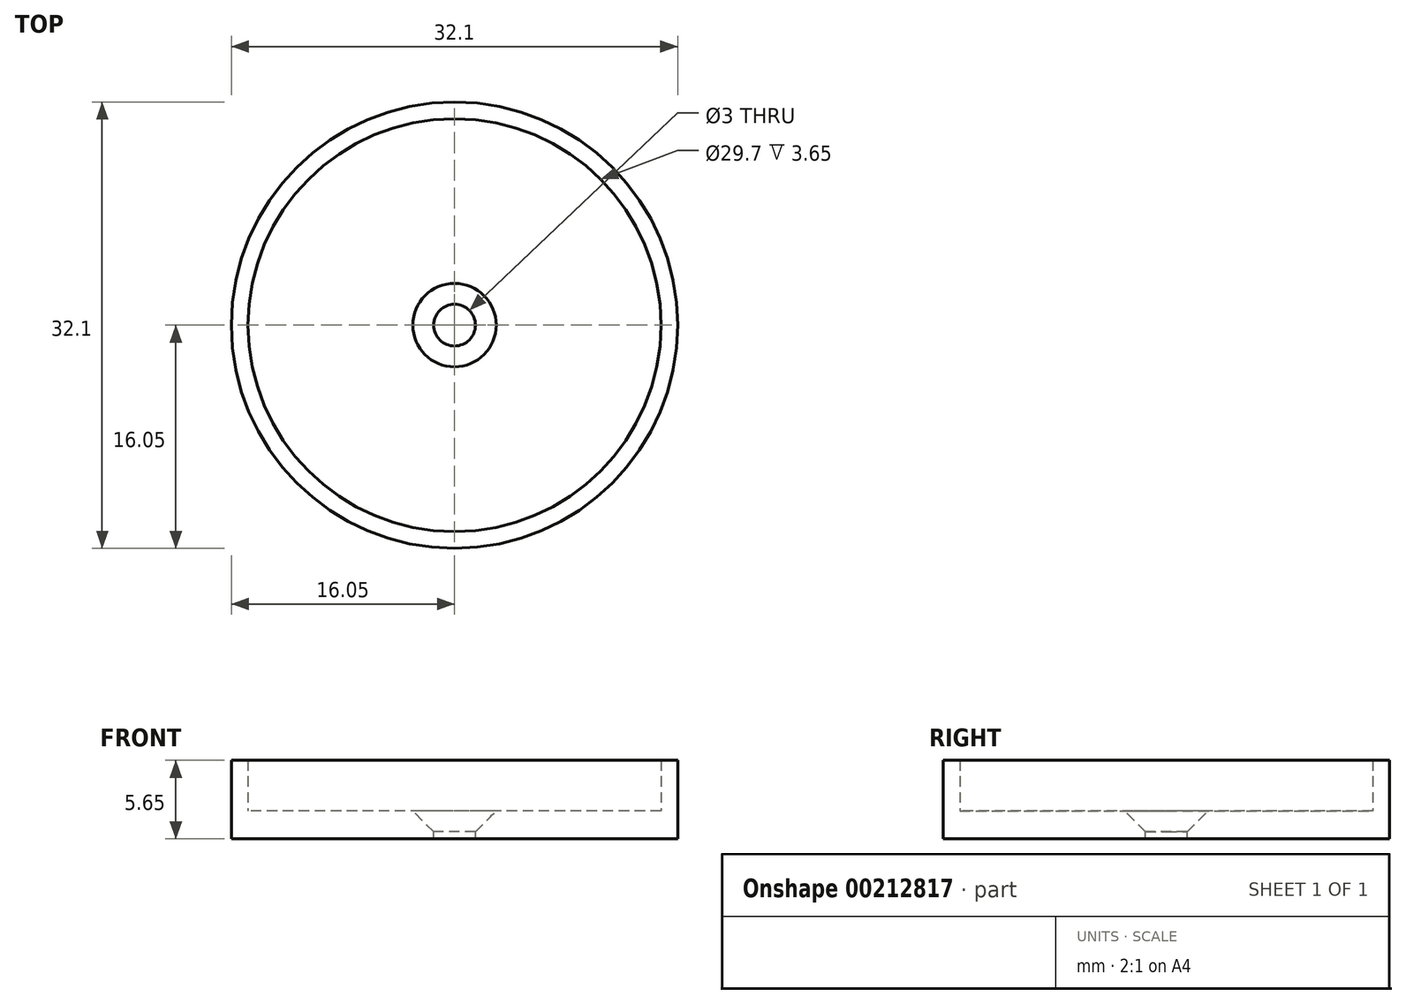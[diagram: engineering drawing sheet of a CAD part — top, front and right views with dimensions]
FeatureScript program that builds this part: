
annotation { "Feature Type Name" : "Feature", "Feature Type Description" : "" }
export const myFeature = defineFeature(function(context is Context, id is Id, definition is map)
    precondition{}
    {
        {
            var Q0;
            Q0=qCreatedBy(makeId("Top.planeOp"),FACE);
            var sketch = newSketch(context, id + "F0", { "sketchPlane" : qUnion([Q0])});
            skCircle(sketch, "E0", {"center": v(0, 0) * mm, "radius": 16.05 * mm});
            skCircle(sketch, "E1", {"center": v(0, 0) * mm, "radius": 14.85 * mm});
            skCircle(sketch, "E2", {"center": v(0, 0) * mm, "radius": 1.5 * mm});
            skSolve(sketch);
        }
        {
            var Q0;
            Q0=makeQuery(id+"F0.imprint","IMPRINT",FACE,{"disambiguationData":[TD([[makeQuery(id+"F0.imprint","IMPRINT",EDGE,{"derivedFrom":sQuery(id+"F0.wireOp",EDGE,"E1")}),1.0]])]});
            var Q1;
            Q1=makeQuery(id+"F0.imprint","IMPRINT",FACE,{"disambiguationData":[TD([[makeQuery(id+"F0.imprint","IMPRINT",EDGE,{"derivedFrom":sQuery(id+"F0.wireOp",EDGE,"E0")}),1.0]])]});
            extrude(context, id + "F1", {"entities" : qUnion([Q0, Q1]), "oppositeDirection" : true, "depth" : 2 * mm, "offsetDistance" : 25 * mm});
        }
        {
            var Q0;
            Q0=makeQuery(id+"F0.imprint","IMPRINT",FACE,{"disambiguationData":[TD([[makeQuery(id+"F0.imprint","IMPRINT",EDGE,{"derivedFrom":sQuery(id+"F0.wireOp",EDGE,"E0")}),1.0]])]});
            extrude(context, id + "F2", {"entities" : qUnion([Q0]), "operationType" : NewBodyOperationType.ADD, "depth" : 3.65 * mm, "offsetDistance" : 25 * mm});
        }
        {
            var Q0;
            Q0=makeQuery(id+"F1.opExtrude","CAP_EDGE",EDGE,{"disambiguationData":[OSD([sQuery(id+"F0.wireOp",EDGE,"E2")])],"isStart":true});
            chamfer(context, id + "F3", {"entities" : qUnion([Q0]), "width" : 1.5 * mm, "tangentPropagation" : true});
        }
    });
